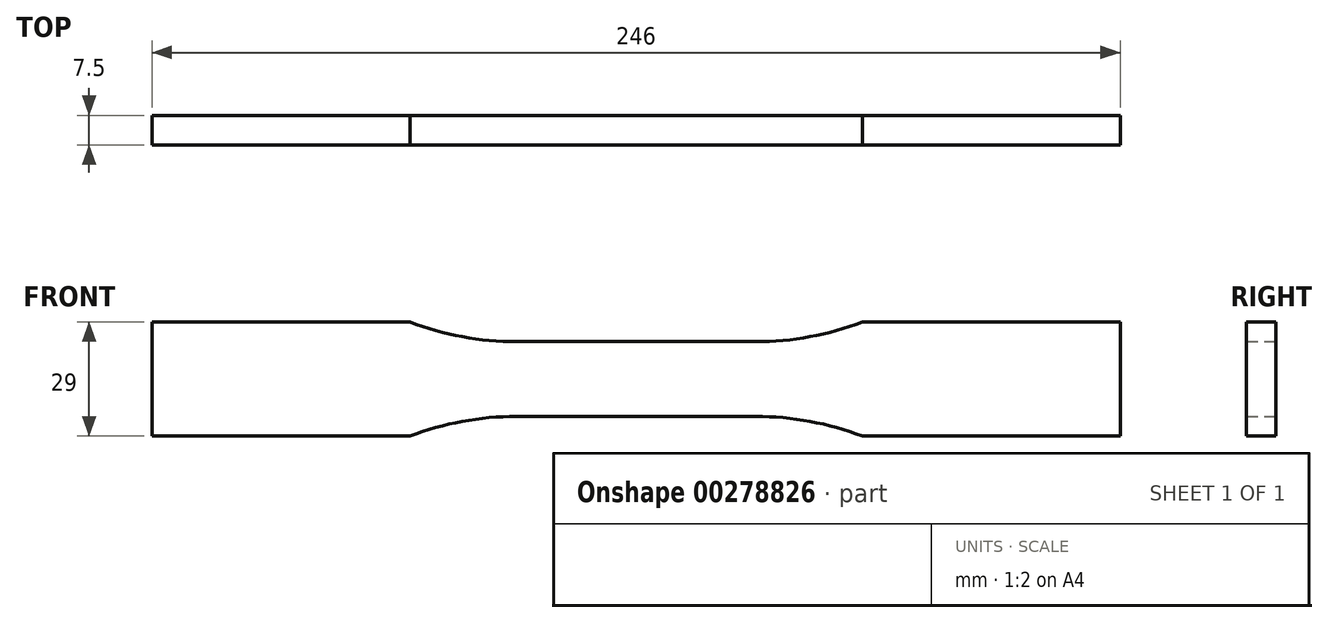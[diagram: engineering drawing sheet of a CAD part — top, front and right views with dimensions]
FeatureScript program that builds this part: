
annotation { "Feature Type Name" : "Feature", "Feature Type Description" : "" }
export const myFeature = defineFeature(function(context is Context, id is Id, definition is map)
    precondition{}
    {
        {
            var Q0;
            Q0=qCreatedBy(makeId("Front.planeOp"),FACE);
            var sketch = newSketch(context, id + "F0", { "sketchPlane" : qUnion([Q0])});
            skLineSegment(sketch, "E0", {"start": v(0, 9.5) * mm, "end": v(30.39, 9.5) * mm});
            skArc(sketch, "E1", {"start": v(30.39, 9.5) * mm, "mid": v(44.17, 10.76) * mm, "end": v(57.5, 14.5) * mm});
            skLineSegment(sketch, "E2", {"start": v(57.5, 14.5) * mm, "end": v(123, 14.5) * mm});
            skLineSegment(sketch, "E3.MirrorCS", {"start": v(0, -9.5) * mm, "end": v(30.39, -9.5) * mm});
            skLineSegment(sketch, "E4.MirrorCS", {"start": v(57.5, -14.5) * mm, "end": v(123, -14.5) * mm});
            skArc(sketch, "E5.MirrorCS", {"start": v(30.39, -9.5) * mm, "mid": v(44.17, -10.76) * mm, "end": v(57.5, -14.5) * mm});
            skLineSegment(sketch, "E6.MirrorCS", {"start": v(-57.5, 14.5) * mm, "end": v(-123, 14.5) * mm});
            skLineSegment(sketch, "E7.MirrorCS", {"start": v(-57.5, -14.5) * mm, "end": v(-123, -14.5) * mm});
            skLineSegment(sketch, "E8.MirrorCS", {"start": v(0, 9.5) * mm, "end": v(-30.39, 9.5) * mm});
            skArc(sketch, "E9.MirrorCS", {"start": v(-30.39, 9.5) * mm, "mid": v(-44.17, 10.76) * mm, "end": v(-57.5, 14.5) * mm});
            skLineSegment(sketch, "E10.MirrorCS", {"start": v(0, -9.5) * mm, "end": v(-30.39, -9.5) * mm});
            skArc(sketch, "E11.MirrorCS", {"start": v(-30.39, -9.5) * mm, "mid": v(-44.17, -10.76) * mm, "end": v(-57.5, -14.5) * mm});
            skLineSegment(sketch, "E12", {"start": v(-123, 14.5) * mm, "end": v(-123, -14.5) * mm});
            skLineSegment(sketch, "E13", {"start": v(123, 14.5) * mm, "end": v(123, -14.5) * mm});
            skSolve(sketch);
        }
        {
            var Q0;
            Q0=makeQuery(id+"F0.imprint","IMPRINT",FACE,{"disambiguationData":[TD([[makeQuery(id+"F0.imprint","IMPRINT",EDGE,{"derivedFrom":sQuery(id+"F0.wireOp",EDGE,"E4.MirrorCS")}),1.0]])]});
            extrude(context, id + "F1", {"entities" : qUnion([Q0]), "endBound" : BoundingType.SYMMETRIC, "depth" : 7.5 * mm});
        }
    });
